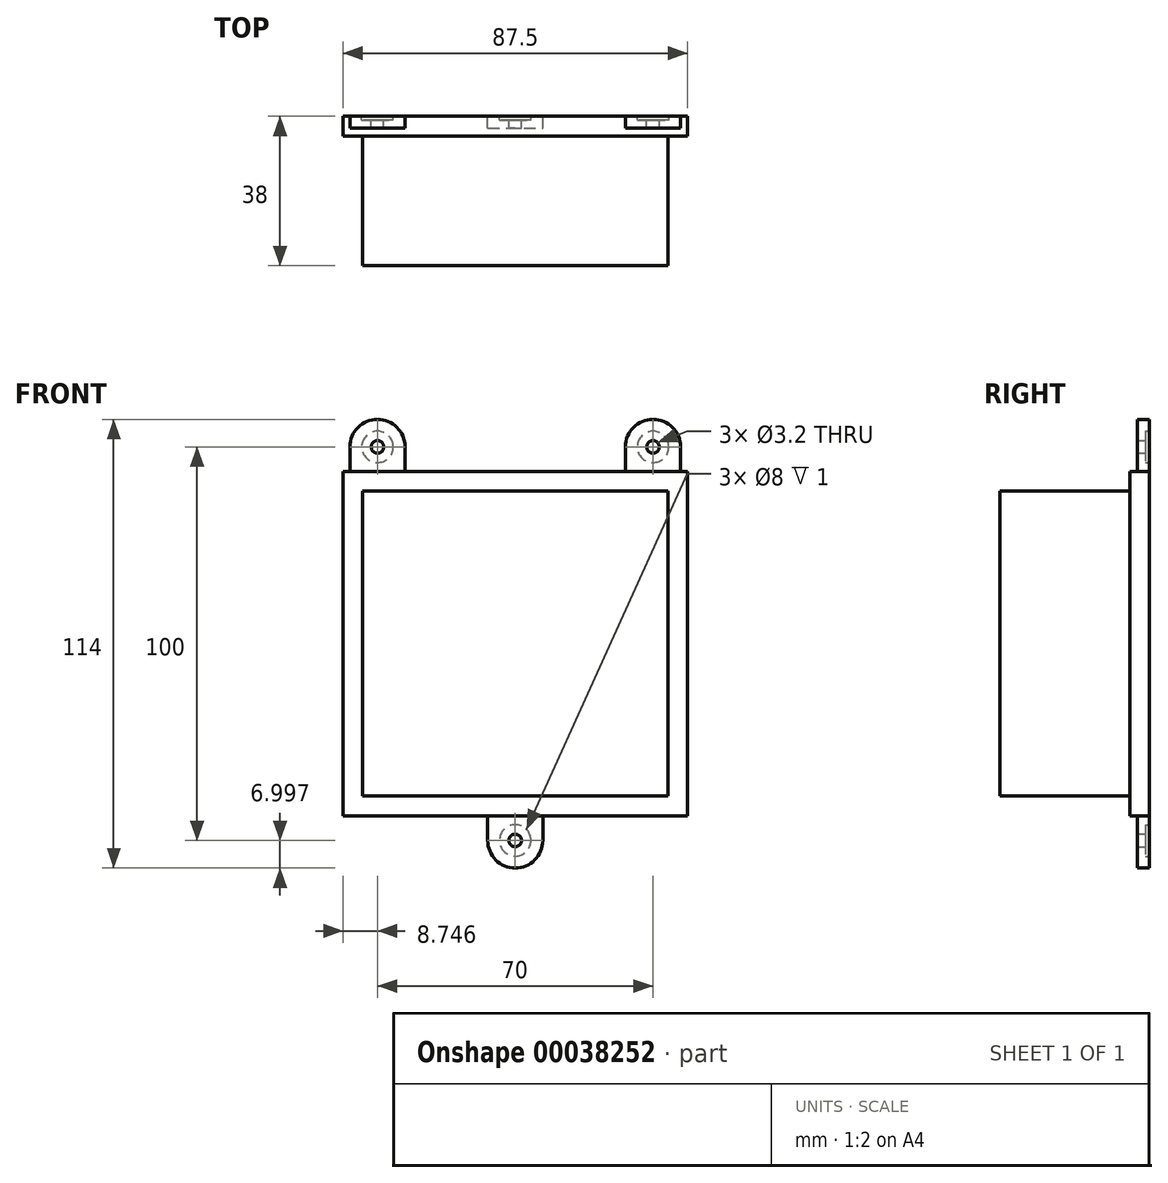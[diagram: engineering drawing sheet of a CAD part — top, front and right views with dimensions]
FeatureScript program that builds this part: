
annotation { "Feature Type Name" : "Feature", "Feature Type Description" : "" }
export const myFeature = defineFeature(function(context is Context, id is Id, definition is map)
    precondition{}
    {
        {
            var Q0;
            Q0=qCreatedBy(makeId("Front.planeOp"),FACE);
            var sketch = newSketch(context, id + "F0", { "sketchPlane" : qUnion([Q0])});
            skLineSegment(sketch, "E0.bottom", {"start": v(-31.9, -41.08) * mm, "end": v(4.86, -41.08) * mm});
            skLineSegment(sketch, "E0.top", {"start": v(-31.9, 46.42) * mm, "end": v(-30.14, 46.42) * mm});
            skLineSegment(sketch, "E0.left", {"start": v(-31.9, -41.08) * mm, "end": v(-31.9, 46.42) * mm});
            skLineSegment(sketch, "E0.right", {"start": v(55.6, -41.08) * mm, "end": v(55.6, 46.42) * mm});
            skPoint(sketch, "E1.startSnap0", {"position": v(-31.9, 2.67) * mm});
            skArc(sketch, "E2", {"start": v(-16.14, 52.67) * mm, "mid": v(-23.14, 59.67) * mm, "end": v(-30.14, 52.67) * mm});
            skArc(sketch, "E3", {"start": v(53.86, 52.67) * mm, "mid": v(46.86, 59.67) * mm, "end": v(39.86, 52.67) * mm});
            skArc(sketch, "E4", {"start": v(4.86, -47.33) * mm, "mid": v(11.86, -54.33) * mm, "end": v(18.86, -47.33) * mm});
            skLineSegment(sketch, "E5", {"start": v(-30.14, 52.67) * mm, "end": v(-30.14, 46.42) * mm});
            skLineSegment(sketch, "E6", {"start": v(-16.14, 52.67) * mm, "end": v(-16.14, 46.42) * mm});
            skLineSegment(sketch, "E7", {"start": v(39.86, 52.67) * mm, "end": v(39.86, 46.42) * mm});
            skLineSegment(sketch, "E8", {"start": v(53.86, 52.67) * mm, "end": v(53.86, 46.42) * mm});
            skLineSegment(sketch, "E9", {"start": v(18.86, -47.33) * mm, "end": v(18.86, -41.08) * mm});
            skLineSegment(sketch, "E10", {"start": v(4.86, -47.33) * mm, "end": v(4.86, -41.08) * mm});
            skLineSegment(sketch, "E11.trimOffspring", {"start": v(-16.14, 46.42) * mm, "end": v(39.86, 46.42) * mm});
            skLineSegment(sketch, "E12.trimOffspring", {"start": v(18.86, -41.08) * mm, "end": v(55.6, -41.08) * mm});
            skLineSegment(sketch, "E13.trimOffspring", {"start": v(53.86, 46.42) * mm, "end": v(55.6, 46.42) * mm});
            skSolve(sketch);
        }
        {
            var Q0;
            Q0=makeQuery(id+"F0.imprint","IMPRINT",FACE,{"disambiguationData":[TD([[makeQuery(id+"F0.imprint","IMPRINT",EDGE,{"derivedFrom":sQuery(id+"F0.wireOp",EDGE,"E0.bottom")}),1.0]])]});
            extrude(context, id + "F1", {"entities" : qUnion([Q0]), "depth" : 3 * mm});
        }
        {
            var Q0;
            Q0=sQuery(id+"F0.wireOp",VERTEX,"E2.center");
            var Q1;
            Q1=sQuery(id+"F0.wireOp",VERTEX,"E3.center");
            var Q2;
            Q2=sQuery(id+"F0.wireOp",VERTEX,"E4.center");
            var Q3;
            Q3=makeQuery(id+"F1.opExtrude","SWEPT_BODY",BODY,{"disambiguationData":[OSD([sQuery(id+"F0.wireOp",EDGE,"E0.bottom"),sQuery(id+"F0.wireOp",EDGE,"E0.top"),sQuery(id+"F0.wireOp",EDGE,"E0.left"),sQuery(id+"F0.wireOp",EDGE,"E0.right"),sQuery(id+"F0.wireOp",EDGE,"E2"),sQuery(id+"F0.wireOp",EDGE,"E3"),sQuery(id+"F0.wireOp",EDGE,"E4"),sQuery(id+"F0.wireOp",EDGE,"E5"),sQuery(id+"F0.wireOp",EDGE,"E6"),sQuery(id+"F0.wireOp",EDGE,"E7"),sQuery(id+"F0.wireOp",EDGE,"E8"),sQuery(id+"F0.wireOp",EDGE,"E9"),sQuery(id+"F0.wireOp",EDGE,"E10"),sQuery(id+"F0.wireOp",EDGE,"E11.trimOffspring"),sQuery(id+"F0.wireOp",EDGE,"E12.trimOffspring"),sQuery(id+"F0.wireOp",EDGE,"E13.trimOffspring")])]});
            hole(context, id + "F2", {"style" : HoleStyle.C_BORE, "holeDiameter" : 3.2 * mm, "cBoreDiameter" : 8 * mm, "cBoreDepth" : 1 * mm, "endStyle" : HoleEndStyle.THROUGH, "oppositeDirection" : true, "locations" : qUnion([Q0, Q1, Q2]), "scope" : qUnion([Q3])});
        }
        {
            var Q0;
            Q0=makeQuery(id+"F1.opExtrude","CAP_FACE",FACE,{"disambiguationData":[OSD([sQuery(id+"F0.wireOp",EDGE,"E0.bottom"),sQuery(id+"F0.wireOp",EDGE,"E0.top"),sQuery(id+"F0.wireOp",EDGE,"E0.left"),sQuery(id+"F0.wireOp",EDGE,"E0.right"),sQuery(id+"F0.wireOp",EDGE,"E2"),sQuery(id+"F0.wireOp",EDGE,"E3"),sQuery(id+"F0.wireOp",EDGE,"E4"),sQuery(id+"F0.wireOp",EDGE,"E5"),sQuery(id+"F0.wireOp",EDGE,"E6"),sQuery(id+"F0.wireOp",EDGE,"E7"),sQuery(id+"F0.wireOp",EDGE,"E8"),sQuery(id+"F0.wireOp",EDGE,"E9"),sQuery(id+"F0.wireOp",EDGE,"E10"),sQuery(id+"F0.wireOp",EDGE,"E11.trimOffspring"),sQuery(id+"F0.wireOp",EDGE,"E12.trimOffspring"),sQuery(id+"F0.wireOp",EDGE,"E13.trimOffspring")])],"isStart":false});
            var sketch = newSketch(context, id + "F3", { "sketchPlane" : qUnion([Q0])});
            skLineSegment(sketch, "E14", {"start": v(-31.9, 46.42) * mm, "end": v(55.6, 46.42) * mm});
            skLineSegment(sketch, "E15", {"start": v(55.6, 46.42) * mm, "end": v(55.6, -41.08) * mm});
            skLineSegment(sketch, "E16", {"start": v(55.6, -41.08) * mm, "end": v(-31.9, -41.08) * mm});
            skLineSegment(sketch, "E17.bottom", {"start": v(-31.9, -41.08) * mm, "end": v(55.6, -41.08) * mm});
            skLineSegment(sketch, "E17.left", {"start": v(-31.9, -41.08) * mm, "end": v(-31.9, 46.42) * mm});
            skLineSegment(sketch, "E17.right", {"start": v(55.6, -41.08) * mm, "end": v(55.6, 46.42) * mm});
            skSolve(sketch);
        }
        {
            var Q0;
            {var subQ0=sQuery(id+"F3.wireOp",EDGE,"E17.left");Q0=makeQuery(id+"F3.imprint","IMPRINT",FACE,{"disambiguationData":[TD([[makeQuery(id+"F3.imprint","IMPRINT",EDGE,{"derivedFrom":subQ0}),-1.0]])]});}
            extrude(context, id + "F4", {"entities" : qUnion([Q0]), "operationType" : NewBodyOperationType.ADD, "depth" : 2 * mm});
        }
        {
            var Q0;
            Q0=makeQuery(id+"F4.opExtrude","CAP_FACE",FACE,{"disambiguationData":[OSD([sQuery(id+"F3.wireOp",EDGE,"E17.bottom"),sQuery(id+"F3.wireOp",EDGE,"E14"),sQuery(id+"F3.wireOp",EDGE,"E17.left"),sQuery(id+"F3.wireOp",EDGE,"E17.right")])],"isStart":false});
            var sketch = newSketch(context, id + "F5", { "sketchPlane" : qUnion([Q0])});
            skLineSegment(sketch, "E18.bottom", {"start": v(-26.9, -36.08) * mm, "end": v(50.6, -36.08) * mm});
            skLineSegment(sketch, "E18.top", {"start": v(-26.9, 41.42) * mm, "end": v(50.6, 41.42) * mm});
            skLineSegment(sketch, "E18.left", {"start": v(-26.9, -36.08) * mm, "end": v(-26.9, 41.42) * mm});
            skLineSegment(sketch, "E18.right", {"start": v(50.6, -36.08) * mm, "end": v(50.6, 41.42) * mm});
            skSolve(sketch);
        }
        {
            var Q0;
            Q0=makeQuery(id+"F5.imprint","IMPRINT",FACE,{"disambiguationData":[TD([[makeQuery(id+"F5.imprint","IMPRINT",EDGE,{"derivedFrom":sQuery(id+"F5.wireOp",EDGE,"E18.bottom")}),1.0]])]});
            extrude(context, id + "F6", {"entities" : qUnion([Q0]), "operationType" : NewBodyOperationType.ADD, "depth" : 33 * mm});
        }
    });
